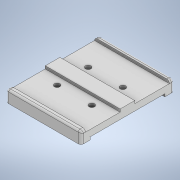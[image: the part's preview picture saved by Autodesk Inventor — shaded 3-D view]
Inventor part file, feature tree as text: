
AUTODESK INVENTOR PART (.ipt)
format: ipt  version: 2021 (Build 250183000, 183)  size: 179,712 bytes
history: native  units: mm
features: sketch x2, extrude x2, fillet x2
ambient origin geometry x8: Origin, YZ Plane, XZ Plane, XY Plane, X Axis, Y Axis, Z Axis, Center Point
bodies: Solid1 (feature_tree)
feature tree (6):
  sketch  "Sketch1"  dims[d0=102.0mm d1=51.0mm d2=3.0mm d3=5.0mm]
  extrude  "Extrusion1"  Depth=3.0mm
  fillet  "Fillet1"  Radius=3.0mm
  fillet  "Fillet2"  Radius=5.0mm
  extrude  "Extrusion2"  Depth=3.0mm
  sketch  "Sketch2"  dims[d4=3.0mm d5=3.0mm d6=43.0mm d7=59.0mm d8=7.0mm d9=10.0mm d10=2.0mm d11=3.0mm d12=82.0mm d13=0.0mm d14=3.0mm d15=3.0mm d16=6.0mm d17=22.0mm d18=34.0mm d19=6.0mm d20=6.0mm d21=6.0mm d22=34.0mm d23=34.0mm d24=34.0mm d25=22.0mm d26=22.0mm d27=22.0mm d28=82.0mm d29=0.0mm]
